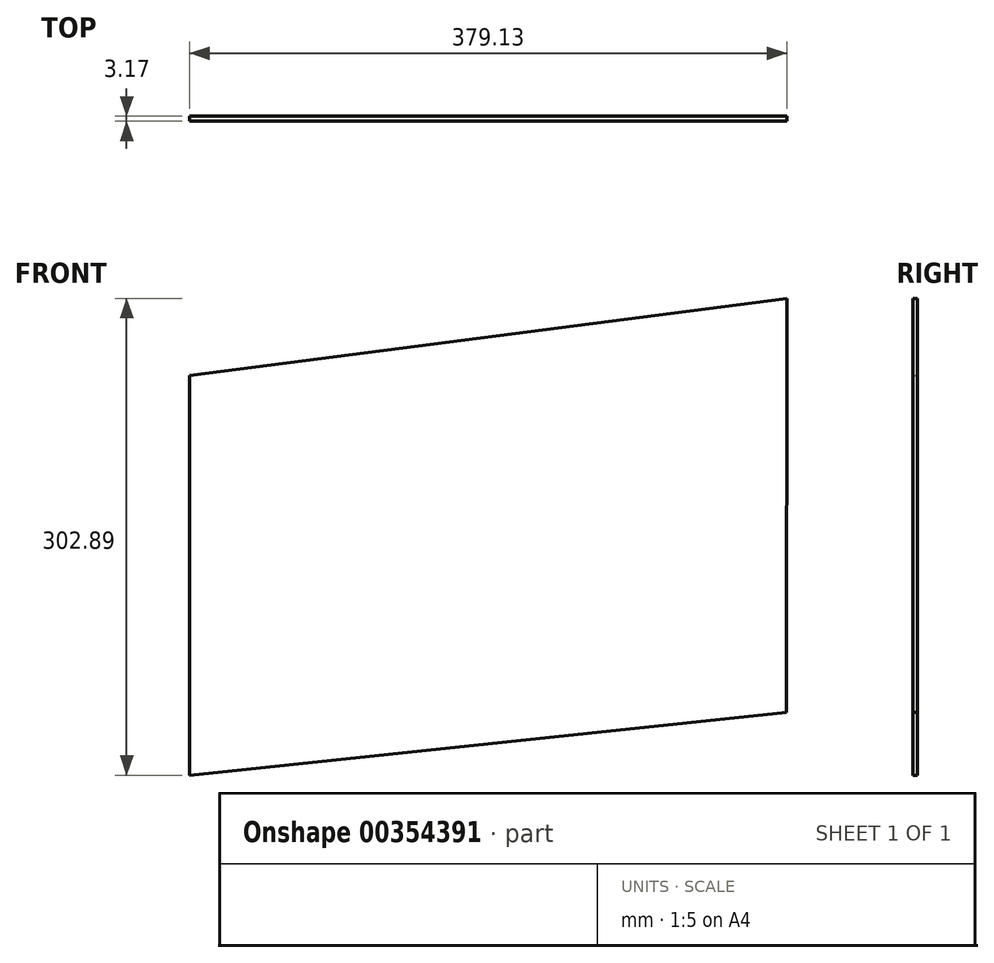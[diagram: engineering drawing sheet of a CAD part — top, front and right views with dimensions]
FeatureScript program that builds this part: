
annotation { "Feature Type Name" : "Feature", "Feature Type Description" : "" }
export const myFeature = defineFeature(function(context is Context, id is Id, definition is map)
    precondition{}
    {
        {
            var Q0;
            Q0=qCreatedBy(makeId("Front.planeOp"),FACE);
            var sketch = newSketch(context, id + "F0", { "sketchPlane" : qUnion([Q0])});
            skLineSegment(sketch, "E0", {"start": v(-268.64, 135.96) * mm, "end": v(-268.64, -118.04) * mm});
            skLineSegment(sketch, "E1", {"start": v(-268.64, -118.04) * mm, "end": v(110.27, -78.22) * mm});
            skLineSegment(sketch, "E2", {"start": v(110.27, -78.22) * mm, "end": v(110.5, 184.85) * mm});
            skLineSegment(sketch, "E3", {"start": v(110.5, 184.85) * mm, "end": v(-268.64, 135.96) * mm});
            skSolve(sketch);
        }
        {
            var Q0;
            Q0 = qSketchRegion(id + "F0", true);
            extrude(context, id + "F1", {"entities" : qUnion([Q0]), "depth" : 3.17 * mm});
        }
    });
